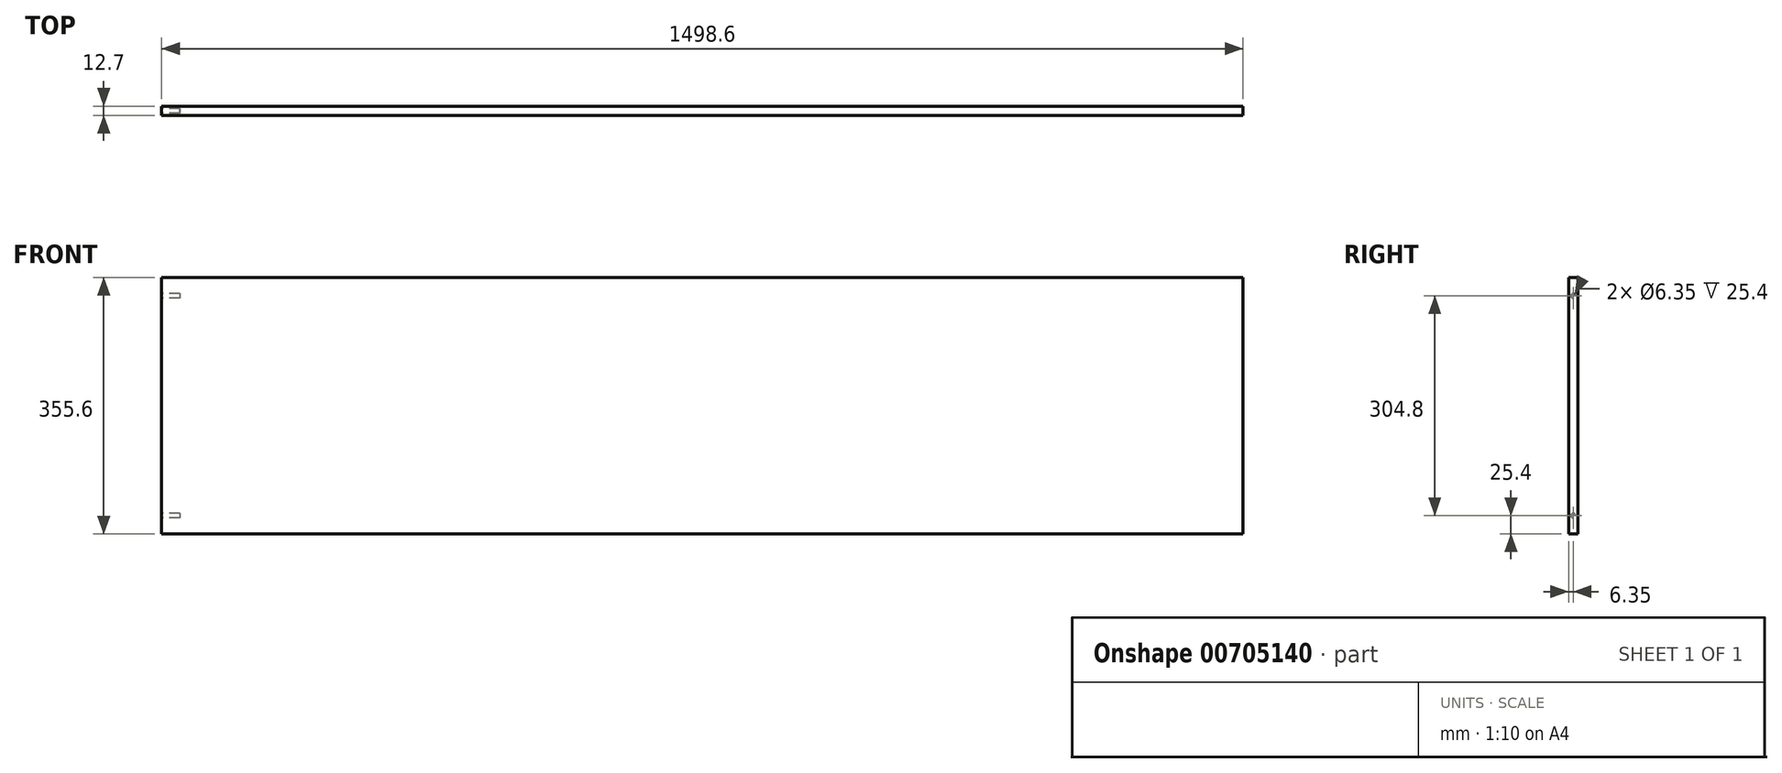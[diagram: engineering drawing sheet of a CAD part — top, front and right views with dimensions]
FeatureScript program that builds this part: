
annotation { "Feature Type Name" : "Feature", "Feature Type Description" : "" }
export const myFeature = defineFeature(function(context is Context, id is Id, definition is map)
    precondition{}
    {
        {
            var Q0;
            Q0=qCreatedBy(makeId("Front.planeOp"),FACE);
            var sketch = newSketch(context, id + "F0", { "sketchPlane" : qUnion([Q0])});
            skLineSegment(sketch, "E0.bottom", {"start": v(749.3, -177.8) * mm, "end": v(-749.3, -177.8) * mm});
            skLineSegment(sketch, "E0.top", {"start": v(749.3, 177.8) * mm, "end": v(-749.3, 177.8) * mm});
            skLineSegment(sketch, "E0.left", {"start": v(749.3, -177.8) * mm, "end": v(749.3, 177.8) * mm});
            skLineSegment(sketch, "E0.right", {"start": v(-749.3, -177.8) * mm, "end": v(-749.3, 177.8) * mm});
            skPoint(sketch, "E0.middle", {"position": v(0, 0) * mm});
            skSolve(sketch);
        }
        {
            var Q0;
            Q0 = qSketchRegion(id + "F0", true);
            extrude(context, id + "F1", {"entities" : qUnion([Q0]), "depth" : 12.7 * mm, "offsetDistance" : 25.4 * mm});
        }
        {
            var Q0;
            Q0=makeQuery(id+"F1.opExtrude","SWEPT_FACE",FACE,{"disambiguationData":[OSD([sQuery(id+"F0.wireOp",EDGE,"E0.right")])]});
            var sketch = newSketch(context, id + "F2", { "sketchPlane" : qUnion([Q0])});
            skCircle(sketch, "E1", {"center": v(6.35, 152.4) * mm, "radius": 3.18 * mm});
            skPoint(sketch, "E1.centerSnap0", {"position": v(6.35, 177.8) * mm});
            skCircle(sketch, "E2", {"center": v(6.35, -152.4) * mm, "radius": 3.18 * mm});
            skPoint(sketch, "E2.centerSnap0", {"position": v(6.35, -177.8) * mm});
            skSolve(sketch);
        }
        {
            var Q0;
            Q0 = qSketchRegion(id + "F2", true);
            extrude(context, id + "F3", {"entities" : qUnion([Q0]), "operationType" : NewBodyOperationType.REMOVE, "oppositeDirection" : true, "depth" : 25.4 * mm, "offsetDistance" : 25.4 * mm});
        }
    });
